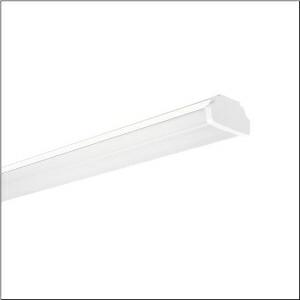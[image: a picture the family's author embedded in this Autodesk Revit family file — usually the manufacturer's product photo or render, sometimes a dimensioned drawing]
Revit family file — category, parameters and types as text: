
# Revit family: modario_r__31_mo_53bm813d2v4085_53ec
name_source: partatom
category: Lighting Fixtures
units: mm (PartAtom-declared; Revit-internal decimal feet)

## family parameters
Cut with Voids When Loaded = No
Host = Face
Light Source = No
Part Type = Normal
Room Calculation Point = No
Round Connector Dimension = Use Diameter
Shared = No

## types (1)
- --- (1 x LED, 8770 lm, 61.8 W, 4000K)
    Apparent Load = 62 VA
    CIE Flux Codes = 61 83 94 92 100
    Color Rendering = 80
    Color Temperature = 4000K
    Default Elevation = 1800 mm
    Description = Modario® 31 MOluminaire insert, length: 1.495mm, width: 81mm, height: 82mm, LED rated luminous flux: 8.770lm, light colour: 840, control gear: DALI 2, control gear: ECG DALI, with plug, 5-pole, with phase selection, mains connection: 220..240V, AC, 50/60Hz, primary optical cover: cover, of PMMA, light emission: direct distribution, primary light characteristic: symmetric, protection rating (complete): IP20, protection rating (LED compartment): IP50, insulation class (complete): insulation class I (protective earthing), certification: CE, ENEC, VDE, UKCA, permissible ambient temperature for indoor applications: -25..+30°C, corresponds to IFS (International Featured Standards) requirements for safety and quality in the food industry, reducing of maximum allowable ambient temperature of 5°C with ceiling mounting, packaging unit: 1 piece
    Height = 92 mm
    Lamp = 1 x LED
    Lamp Light Flux = 8770 lm
    Lamp Power = 61.8 W
    Lamp count = 1
    Length = 1495 mm
    Luminous efficacy = 142 lm/W
    Manufacturer = Siteco
    ModVariant = No
    Model = 53BM813D2V4085
    Mounting Place = Ceiling
    Mounting Type = Pendant
    Number of Poles = 1
    OnlyDefault = Yes
    Power Factor = 1
    Product Name = Modario® 31 MO
    Product group = luminaire insert
    ProductGroupID = 902
    Protection Class = Protection class I
    Protection Degree = IP 20
    RLX_Detail_Level = 1
    RlxData = <blob elided: 42297 chars, md5=7bbcd17f>
    Socket = socket
    Standby Power = 0 W
    System Light Flux = 8770 lm
    System Power = 62 W
    Type Comments = factory setting: luminous flux: 100 % | dim-lin: 254 | 500 mA
    Type Image = l_1003447.jpg
    URL = http://relux.com
    VarID = @adj_117459
    Voltage = 0 V
    Weight = 0.00 kg
    Width = 81 mm

## geometry (parser evidence)
native form markers: Blend x4, Sweep x12
no freeform markers — native parametric forms only
